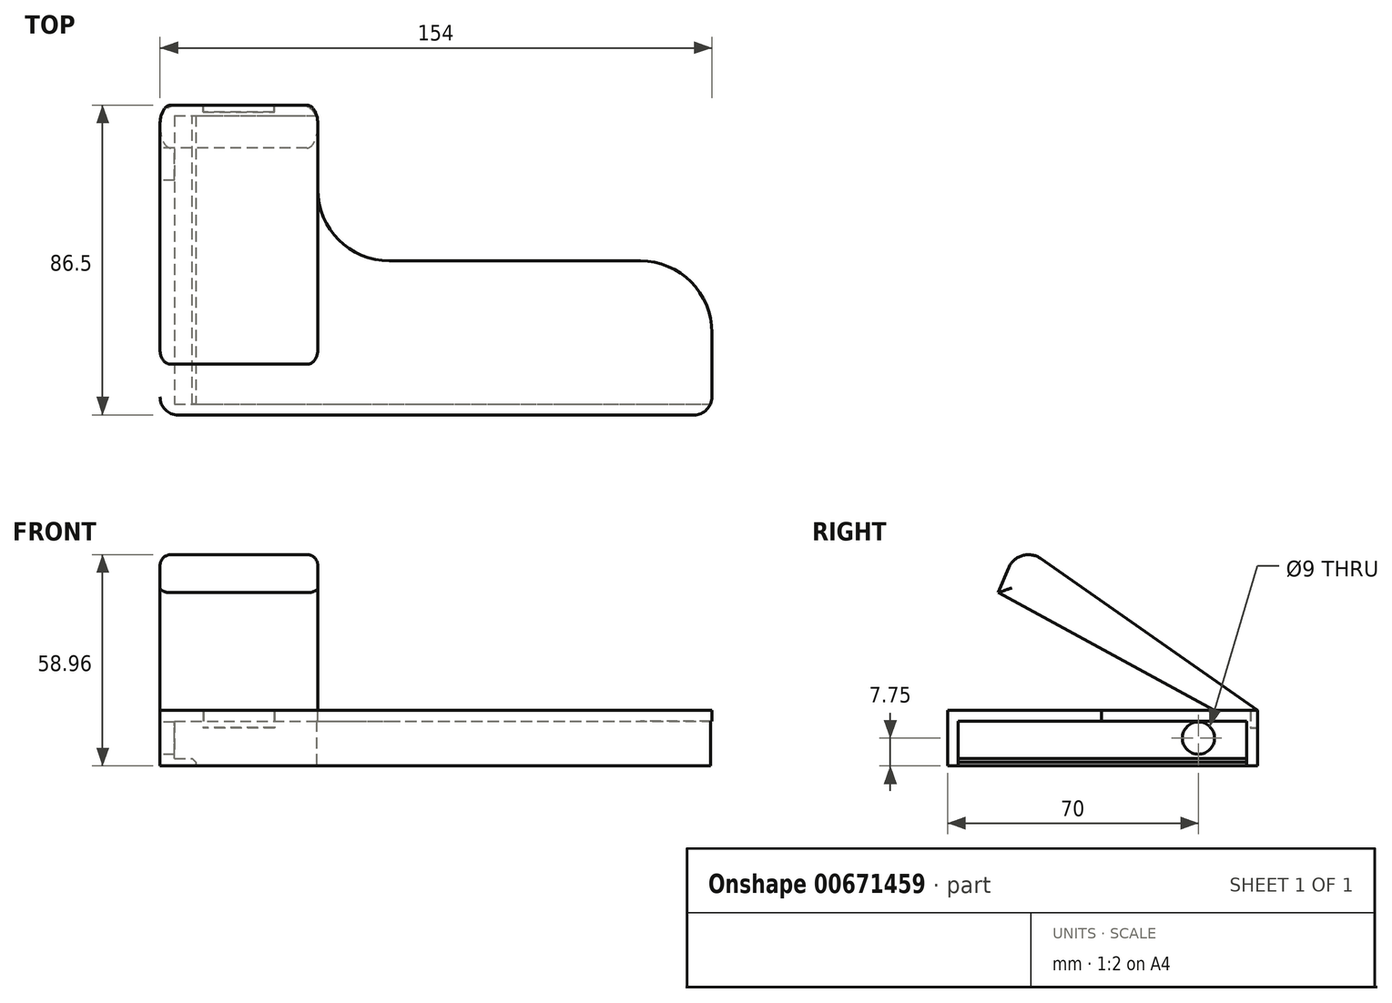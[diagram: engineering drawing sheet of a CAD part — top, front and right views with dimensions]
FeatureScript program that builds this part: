
annotation { "Feature Type Name" : "Feature", "Feature Type Description" : "" }
export const myFeature = defineFeature(function(context is Context, id is Id, definition is map)
    precondition{}
    {
        {
            var Q0;
            Q0=qCreatedBy(makeId("Top.planeOp"),FACE);
            var sketch = newSketch(context, id + "F0", { "sketchPlane" : qUnion([Q0])});
            skLineSegment(sketch, "E0.bottom", {"start": v(-4.93, 0) * mm, "end": v(35.07, 0) * mm});
            skLineSegment(sketch, "E0.top", {"start": v(-4.93, 80.5) * mm, "end": v(35.07, 80.5) * mm});
            skLineSegment(sketch, "E0.left", {"start": v(-4.93, 0) * mm, "end": v(-4.93, 80.5) * mm});
            skLineSegment(sketch, "E0.right", {"start": v(35.07, 60) * mm, "end": v(35.07, 80.5) * mm});
            skLineSegment(sketch, "E1.bottom", {"start": v(55.07, 40) * mm, "end": v(125.07, 40) * mm});
            skLineSegment(sketch, "E1.top", {"start": v(-4.93, 0) * mm, "end": v(145.07, 0) * mm});
            skLineSegment(sketch, "E1.right", {"start": v(145.07, 20) * mm, "end": v(145.07, 0) * mm});
            skPoint(sketch, "E2.visualSharp", {"position": v(35.07, 40) * mm});
            skArc(sketch, "E2.filletArc", {"start": v(35.07, 60) * mm, "mid": v(40.92, 45.86) * mm, "end": v(55.07, 40) * mm});
            skPoint(sketch, "E3.visualSharp", {"position": v(145.07, 40) * mm});
            skArc(sketch, "E3.filletArc", {"start": v(145.07, 20) * mm, "mid": v(139.2, 34.14) * mm, "end": v(125.07, 40) * mm});
            skLineSegment(sketch, "E4.top", {"start": v(-4.93, 83.5) * mm, "end": v(35.07, 83.5) * mm});
            skLineSegment(sketch, "E4.left", {"start": v(-4.93, 80.5) * mm, "end": v(-4.93, 83.5) * mm});
            skLineSegment(sketch, "E4.right", {"start": v(35.07, 80.5) * mm, "end": v(35.07, 83.5) * mm});
            skLineSegment(sketch, "E5.top", {"start": v(-4.93, -3) * mm, "end": v(145.07, -3) * mm});
            skLineSegment(sketch, "E5.left", {"start": v(-4.93, 0) * mm, "end": v(-4.93, -3) * mm});
            skLineSegment(sketch, "E5.right", {"start": v(145.07, 0) * mm, "end": v(145.07, -3) * mm});
            skSolve(sketch);
        }
        {
            var Q0;
            Q0=makeQuery(id+"F0.imprint","IMPRINT",FACE,{"disambiguationData":[TD([[makeQuery(id+"F0.imprint","IMPRINT",EDGE,{"derivedFrom":sQuery(id+"F0.wireOp",EDGE,"E0.bottom")}),1.0]])]});
            extrude(context, id + "F1", {"entities" : qUnion([Q0]), "oppositeDirection" : true, "depth" : 3 * mm, "offsetDistance" : 25 * mm});
        }
        {
            var Q0;
            Q0=makeQuery(id+"F0.imprint","IMPRINT",FACE,{"disambiguationData":[TD([[makeQuery(id+"F0.imprint","IMPRINT",EDGE,{"derivedFrom":sQuery(id+"F0.wireOp",EDGE,"E0.top")}),1.0]])]});
            var Q1;
            Q1=makeQuery(id+"F0.imprint","IMPRINT",FACE,{"disambiguationData":[TD([[makeQuery(id+"F0.imprint","IMPRINT",EDGE,{"derivedFrom":sQuery(id+"F0.wireOp",EDGE,"E0.bottom")}),-1.0]])]});
            extrude(context, id + "F2", {"entities" : qUnion([Q0, Q1]), "operationType" : NewBodyOperationType.ADD, "oppositeDirection" : true, "depth" : 15.5 * mm, "offsetDistance" : 25 * mm});
        }
        {
            var Q0;
            Q0=makeQuery(id+"F2.boolean.opBoolean","MERGE",FACE,{"derivedFrom":[makeQuery(id+"F1.opExtrude","SWEPT_FACE",FACE,{"disambiguationData":[OSD([sQuery(id+"F0.wireOp",EDGE,"E0.left")])]}),makeQuery(id+"F2.opExtrude","SWEPT_FACE",FACE,{"disambiguationData":[OSD([sQuery(id+"F0.wireOp",EDGE,"E4.left")])]}),makeQuery(id+"F2.opExtrude","SWEPT_FACE",FACE,{"disambiguationData":[OSD([sQuery(id+"F0.wireOp",EDGE,"E5.left")])]})]});
            var sketch = newSketch(context, id + "F3", { "sketchPlane" : qUnion([Q0])});
            skLineSegment(sketch, "E6.bottom", {"start": v(-83.5, -15.5) * mm, "end": v(3, -15.5) * mm});
            skLineSegment(sketch, "E6.top", {"start": v(-83.5, 0) * mm, "end": v(3, 0) * mm});
            skLineSegment(sketch, "E6.left", {"start": v(-83.5, -15.5) * mm, "end": v(-83.5, 0) * mm});
            skLineSegment(sketch, "E6.right", {"start": v(3, -15.5) * mm, "end": v(3, 0) * mm});
            skSolve(sketch);
        }
        {
            var Q0;
            {var subQ1=sQuery(id+"F0.wireOp",EDGE,"E0.left");Q0=makeQuery(id+"F3.imprint","IMPRINT",FACE,{"disambiguationData":[TD([[makeQuery(id+"F3.imprint","IMPRINT",EDGE,{"derivedFrom":makeQuery(id+"F1.opExtrude","CAP_EDGE",EDGE,{"disambiguationData":[OSD([subQ1])],"isStart":false})}),1.0]])]});}
            var Q1;
            Q1=makeQuery(id+"F3.imprint","IMPRINT",FACE,{"disambiguationData":[TD([[makeQuery(id+"F3.imprint","IMPRINT",EDGE,{"derivedFrom":sQuery(id+"F3.wireOp",EDGE,"E6.top")}),1.0]])]});
            extrude(context, id + "F4", {"entities" : qUnion([Q0, Q1]), "operationType" : NewBodyOperationType.ADD, "depth" : 4 * mm, "offsetDistance" : 25 * mm});
        }
        {
            var Q0;
            Q0=makeQuery(id+"F4.boolean.opBoolean","MERGE",FACE,{"derivedFrom":[makeQuery(id+"F2.opExtrude","CAP_FACE",FACE,{"disambiguationData":[OSD([sQuery(id+"F0.wireOp",EDGE,"E0.bottom"),sQuery(id+"F0.wireOp",EDGE,"E1.top"),sQuery(id+"F0.wireOp",EDGE,"E5.top"),sQuery(id+"F0.wireOp",EDGE,"E5.left"),sQuery(id+"F0.wireOp",EDGE,"E5.right")])],"isStart":false}),makeQuery(id+"F2.opExtrude","CAP_FACE",FACE,{"disambiguationData":[OSD([sQuery(id+"F0.wireOp",EDGE,"E0.top"),sQuery(id+"F0.wireOp",EDGE,"E4.top"),sQuery(id+"F0.wireOp",EDGE,"E4.left"),sQuery(id+"F0.wireOp",EDGE,"E4.right")])],"isStart":false}),makeQuery(id+"F4.opExtrude","SWEPT_FACE",FACE,{"disambiguationData":[OSD([sQuery(id+"F3.wireOp",EDGE,"E6.bottom")])]})]});
            var sketch = newSketch(context, id + "F5", { "sketchPlane" : qUnion([Q0])});
            skLineSegment(sketch, "E7.bottom", {"start": v(-8.93, -83.5) * mm, "end": v(1.07, -83.5) * mm});
            skLineSegment(sketch, "E7.top", {"start": v(-8.93, 3) * mm, "end": v(1.07, 3) * mm});
            skLineSegment(sketch, "E7.left", {"start": v(-8.93, -83.5) * mm, "end": v(-8.93, 3) * mm});
            skLineSegment(sketch, "E7.right", {"start": v(1.07, -83.5) * mm, "end": v(1.07, 3) * mm});
            skSolve(sketch);
        }
        {
            var Q0;
            {var subQ5=makeQuery(id+"F4.opExtrude","CAP_EDGE",EDGE,{"disambiguationData":[OSD([sQuery(id+"F3.wireOp",EDGE,"E6.bottom")])],"isStart":true});Q0=makeQuery(id+"F5.imprint","IMPRINT",FACE,{"disambiguationData":[TD([[makeQuery(id+"F5.imprint","IMPRINT",EDGE,{"derivedFrom":subQ5}),-1.0]])]});}
            extrude(context, id + "F6", {"entities" : qUnion([Q0]), "operationType" : NewBodyOperationType.ADD, "oppositeDirection" : true, "depth" : 2 * mm, "offsetDistance" : 25 * mm});
        }
        {
            var Q0;
            Q0=makeQuery(id+"F4.opExtrude","CAP_FACE",FACE,{"disambiguationData":[OSD([sQuery(id+"F3.wireOp",EDGE,"E6.bottom"),sQuery(id+"F3.wireOp",EDGE,"E6.top"),sQuery(id+"F3.wireOp",EDGE,"E6.left"),sQuery(id+"F3.wireOp",EDGE,"E6.right")])],"isStart":false});
            var sketch = newSketch(context, id + "F7", { "sketchPlane" : qUnion([Q0])});
            skCircle(sketch, "E8", {"center": v(-67, -7.75) * mm, "radius": 4.5 * mm});
            skLineSegment(sketch, "E9", {"start": v(-83.5, -7.75) * mm, "end": v(-67, -7.75) * mm, "construction": true});
            skSolve(sketch);
        }
        {
            var Q0;
            Q0=makeQuery(id+"F7.imprint","IMPRINT",FACE,{"disambiguationData":[TD([[makeQuery(id+"F7.imprint","IMPRINT",EDGE,{"derivedFrom":sQuery(id+"F7.wireOp",EDGE,"E8")}),1.0]])]});
            extrude(context, id + "F8", {"entities" : qUnion([Q0]), "operationType" : NewBodyOperationType.REMOVE, "oppositeDirection" : true, "depth" : 25 * mm, "offsetDistance" : 25 * mm});
        }
        {
            var Q0;
            Q0=makeQuery(id+"F4.opExtrude","CAP_FACE",FACE,{"disambiguationData":[OSD([sQuery(id+"F3.wireOp",EDGE,"E6.bottom"),sQuery(id+"F3.wireOp",EDGE,"E6.top"),sQuery(id+"F3.wireOp",EDGE,"E6.left"),sQuery(id+"F3.wireOp",EDGE,"E6.right")])],"isStart":false});
            var sketch = newSketch(context, id + "F9", { "sketchPlane" : qUnion([Q0])});
            skLineSegment(sketch, "E10", {"start": v(-83.5, 0) * mm, "end": v(-9.85, 51.57) * mm});
            skLineSegment(sketch, "E11", {"start": v(3, 40.57) * mm, "end": v(3, 0) * mm, "construction": true});
            skLineSegment(sketch, "E12", {"start": v(-71.5, 0) * mm, "end": v(-9.85, 33.57) * mm});
            skPoint(sketch, "E13.end.orphan", {"position": v(3, 60.57) * mm});
            skLineSegment(sketch, "E14", {"start": v(-9.85, 51.57) * mm, "end": v(-9.85, 33.57) * mm});
            skLineSegment(sketch, "E15", {"start": v(-23.27, 26.27) * mm, "end": v(-32.62, 35.62) * mm});
            skLineSegment(sketch, "E16", {"start": v(3, -1.56) * mm, "end": v(-27.19, 71.78) * mm});
            skSolve(sketch);
        }
        {
            var Q0;
            {var subQ3=sQuery(id+"F9.wireOp",EDGE,"E15");Q0=makeQuery(id+"F9.imprint","IMPRINT",FACE,{"disambiguationData":[TD([[makeQuery(id+"F9.imprint","IMPRINT",EDGE,{"derivedFrom":subQ3}),1.0]])]});}
            var Q1;
            {var subQ0=sQuery(id+"F9.wireOp",EDGE,"E15");Q1=makeQuery(id+"F9.imprint","IMPRINT",FACE,{"disambiguationData":[TD([[makeQuery(id+"F9.imprint","IMPRINT",EDGE,{"derivedFrom":subQ0}),-1.0]])]});}
            extrude(context, id + "F10", {"entities" : qUnion([Q0, Q1]), "oppositeDirection" : true, "depth" : 44 * mm, "offsetDistance" : 25 * mm});
        }
        {
            var Q0;
            Q0=makeQuery(id+"F4.boolean.opBoolean","MERGE",FACE,{"derivedFrom":[makeQuery(id+"F2.opExtrude","SWEPT_FACE",FACE,{"disambiguationData":[OSD([sQuery(id+"F0.wireOp",EDGE,"E4.top")])]}),makeQuery(id+"F4.opExtrude","SWEPT_FACE",FACE,{"disambiguationData":[OSD([sQuery(id+"F3.wireOp",EDGE,"E6.left")])]})]});
            var sketch = newSketch(context, id + "F11", { "sketchPlane" : qUnion([Q0])});
            skLineSegment(sketch, "E17.bottom", {"start": v(-23.07, 0) * mm, "end": v(-3.07, 0) * mm});
            skLineSegment(sketch, "E17.top", {"start": v(-23.07, -5) * mm, "end": v(-3.07, -5) * mm});
            skLineSegment(sketch, "E17.left", {"start": v(-23.07, 0) * mm, "end": v(-23.07, -5) * mm});
            skLineSegment(sketch, "E17.right", {"start": v(-3.07, 0) * mm, "end": v(-3.07, -5) * mm});
            skPoint(sketch, "E18", {"position": v(-13.07, 0) * mm});
            skSolve(sketch);
        }
        {
            var Q0;
            Q0=makeQuery(id+"F11.imprint","IMPRINT",FACE,{"disambiguationData":[TD([[makeQuery(id+"F11.imprint","IMPRINT",EDGE,{"derivedFrom":sQuery(id+"F11.wireOp",EDGE,"E17.bottom")}),1.0]])]});
            extrude(context, id + "F12", {"entities" : qUnion([Q0]), "operationType" : NewBodyOperationType.REMOVE, "oppositeDirection" : true, "depth" : 2 * mm, "offsetDistance" : 25 * mm});
        }
        {
            var Q0;
            Q0=makeQuery(id+"F4.boolean.opBoolean","MERGE",FACE,{"derivedFrom":[makeQuery(id+"F2.opExtrude","SWEPT_FACE",FACE,{"disambiguationData":[OSD([sQuery(id+"F0.wireOp",EDGE,"E4.top")])]}),makeQuery(id+"F4.opExtrude","SWEPT_FACE",FACE,{"disambiguationData":[OSD([sQuery(id+"F3.wireOp",EDGE,"E6.left")])]})]});
            var sketch = newSketch(context, id + "F13", { "sketchPlane" : qUnion([Q0])});
            skLineSegment(sketch, "E19.0", {"start": v(-3.27, 0) * mm, "end": v(-3.27, -4.8) * mm});
            skLineSegment(sketch, "E19.1", {"start": v(-22.87, -4.8) * mm, "end": v(-3.27, -4.8) * mm});
            skLineSegment(sketch, "E19.2", {"start": v(-22.87, 0) * mm, "end": v(-22.87, -4.8) * mm});
            skLineSegment(sketch, "E20", {"start": v(-22.87, 0) * mm, "end": v(-3.27, 0) * mm});
            skSolve(sketch);
        }
        {
            var Q0;
            Q0=makeQuery(id+"F13.imprint","IMPRINT",FACE,{"disambiguationData":[TD([[makeQuery(id+"F13.imprint","IMPRINT",EDGE,{"derivedFrom":sQuery(id+"F13.wireOp",EDGE,"E19.0")}),-1.0]])]});
            extrude(context, id + "F14", {"entities" : qUnion([Q0]), "operationType" : NewBodyOperationType.ADD, "oppositeDirection" : true, "depth" : 1.9 * mm, "offsetDistance" : 25 * mm});
        }
        {
            var Q0;
            Q0=makeQuery(id+"F10.opExtrude","SWEPT_EDGE",EDGE,{"disambiguationData":[OSD([sQuery(id+"F9.wireOp",EDGE,"E10"),sQuery(id+"F9.wireOp",EDGE,"E16")])]});
            fillet(context, id + "F15", {"entities" : qUnion([Q0]), "radius" : 6 * mm, "tangentPropagation" : true, "allowEdgeOverflow" : false});
        }
        {
            var Q0;
            Q0=makeQuery(id+"F10.opExtrude","CAP_EDGE",EDGE,{"disambiguationData":[OSD([sQuery(id+"F9.wireOp",EDGE,"E10")])],"isStart":true});
            var Q1;
            Q1=makeQuery(id+"F10.opExtrude","CAP_EDGE",EDGE,{"disambiguationData":[OSD([sQuery(id+"F9.wireOp",EDGE,"E10")])],"isStart":false});
            var Q2;
            Q2=makeQuery(id+"F10.opExtrude","CAP_EDGE",EDGE,{"disambiguationData":[OSD([sQuery(id+"F9.wireOp",EDGE,"E12")])],"isStart":true});
            var Q3;
            Q3=makeQuery(id+"F10.opExtrude","CAP_EDGE",EDGE,{"disambiguationData":[OSD([sQuery(id+"F9.wireOp",EDGE,"E12")])],"isStart":false});
            fillet(context, id + "F16", {"entities" : qUnion([Q0, Q1, Q2, Q3]), "radius" : 3 * mm, "tangentPropagation" : true, "allowEdgeOverflow" : false});
        }
        {
            var Q0;
            Q0=makeQuery(id+"F4.opExtrude","CAP_EDGE",EDGE,{"disambiguationData":[OSD([sQuery(id+"F3.wireOp",EDGE,"E6.left")])],"isStart":false});
            var Q1;
            Q1=makeQuery(id+"F2.opExtrude","SWEPT_EDGE",EDGE,{"disambiguationData":[OSD([sQuery(id+"F0.wireOp",EDGE,"E4.top"),sQuery(id+"F0.wireOp",EDGE,"E4.right")])]});
            fillet(context, id + "F17", {"entities" : qUnion([Q0, Q1]), "radius" : 5 * mm, "tangentPropagation" : true, "allowEdgeOverflow" : false});
        }
        {
            var Q0;
            Q0=makeQuery(id+"F6.opExtrude","CAP_EDGE",EDGE,{"disambiguationData":[OSD([sQuery(id+"F5.wireOp",EDGE,"E7.right")])],"isStart":false});
            chamfer(context, id + "F18", {"entities" : qUnion([Q0]), "width" : 1 * mm, "tangentPropagation" : true});
        }
        {
            var Q0;
            Q0=makeQuery(id+"F4.opExtrude","CAP_EDGE",EDGE,{"disambiguationData":[OSD([sQuery(id+"F3.wireOp",EDGE,"E6.right")])],"isStart":false});
            fillet(context, id + "F19", {"entities" : qUnion([Q0]), "radius" : 5 * mm, "tangentPropagation" : true, "allowEdgeOverflow" : false});
        }
        {
            var Q0;
            Q0=makeQuery(id+"F2.opExtrude","SWEPT_EDGE",EDGE,{"disambiguationData":[OSD([sQuery(id+"F0.wireOp",EDGE,"E5.top"),sQuery(id+"F0.wireOp",EDGE,"E5.right")])]});
            fillet(context, id + "F20", {"entities" : qUnion([Q0]), "radius" : 5 * mm, "tangentPropagation" : true, "allowEdgeOverflow" : false});
        }
    });
